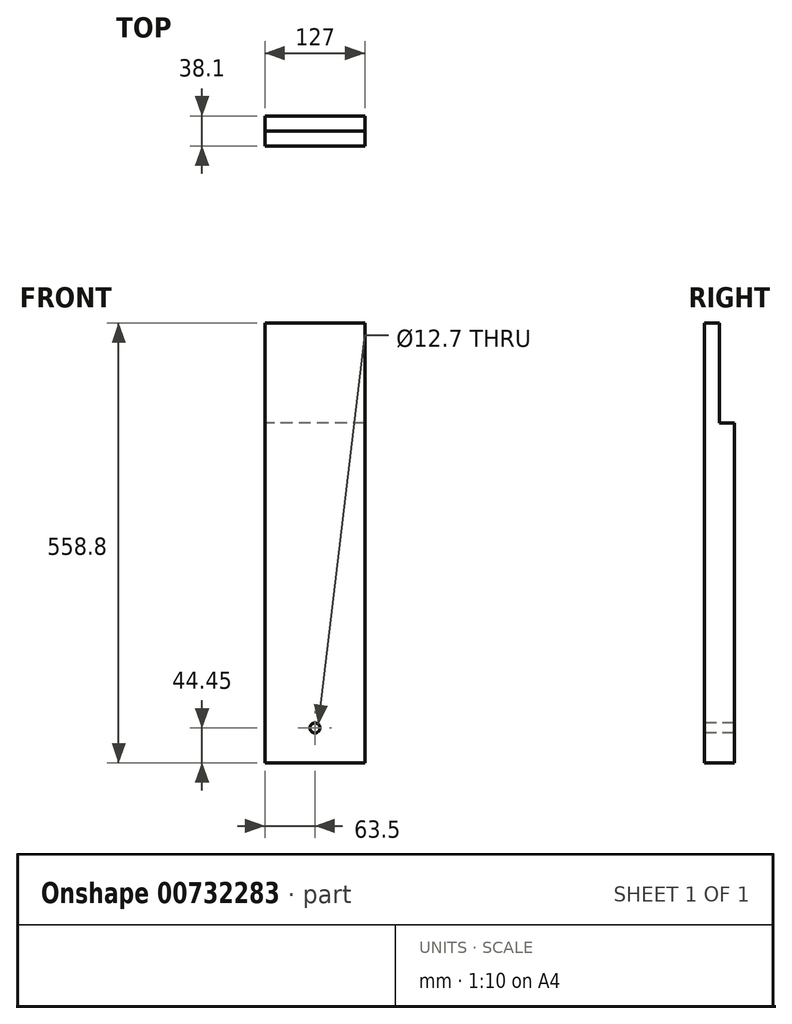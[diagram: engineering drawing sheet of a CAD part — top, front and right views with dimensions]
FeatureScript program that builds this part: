
annotation { "Feature Type Name" : "Feature", "Feature Type Description" : "" }
export const myFeature = defineFeature(function(context is Context, id is Id, definition is map)
    precondition{}
    {
        {
            var Q0;
            Q0=qCreatedBy(makeId("Front.planeOp"),FACE);
            var sketch = newSketch(context, id + "F0", { "sketchPlane" : qUnion([Q0])});
            skLineSegment(sketch, "E0.bottom", {"start": v(63.5, 279.4) * mm, "end": v(-63.5, 279.4) * mm});
            skLineSegment(sketch, "E0.top", {"start": v(63.5, -279.4) * mm, "end": v(-63.5, -279.4) * mm});
            skLineSegment(sketch, "E0.left", {"start": v(63.5, 279.4) * mm, "end": v(63.5, -279.4) * mm});
            skLineSegment(sketch, "E0.right", {"start": v(-63.5, 279.4) * mm, "end": v(-63.5, -279.4) * mm});
            skPoint(sketch, "E0.middle", {"position": v(0, 0) * mm});
            skSolve(sketch);
        }
        {
            var Q0;
            Q0 = qSketchRegion(id + "F0", true);
            extrude(context, id + "F1", {"entities" : qUnion([Q0]), "depth" : 38.1 * mm, "offsetDistance" : 25.4 * mm});
        }
        {
            var Q0;
            Q0=makeQuery(id+"F1.opExtrude","SWEPT_FACE",FACE,{"disambiguationData":[OSD([sQuery(id+"F0.wireOp",EDGE,"E0.right")])]});
            var sketch = newSketch(context, id + "F2", { "sketchPlane" : qUnion([Q0])});
            skLineSegment(sketch, "E1.bottom", {"start": v(19.05, 279.4) * mm, "end": v(0, 279.4) * mm});
            skLineSegment(sketch, "E1.top", {"start": v(19.05, 152.4) * mm, "end": v(0, 152.4) * mm});
            skLineSegment(sketch, "E1.left", {"start": v(19.05, 279.4) * mm, "end": v(19.05, 152.4) * mm});
            skLineSegment(sketch, "E1.right", {"start": v(0, 279.4) * mm, "end": v(0, 152.4) * mm});
            skSolve(sketch);
        }
        {
            var Q0;
            Q0 = qSketchRegion(id + "F2", true);
            extrude(context, id + "F3", {"entities" : qUnion([Q0]), "operationType" : NewBodyOperationType.REMOVE, "oppositeDirection" : true, "depth" : 152.4 * mm, "offsetDistance" : 25.4 * mm});
        }
        {
            var Q0;
            Q0=makeQuery(id+"F1.opExtrude","CAP_FACE",FACE,{"disambiguationData":[OSD([sQuery(id+"F0.wireOp",EDGE,"E0.bottom"),sQuery(id+"F0.wireOp",EDGE,"E0.top"),sQuery(id+"F0.wireOp",EDGE,"E0.left"),sQuery(id+"F0.wireOp",EDGE,"E0.right")])],"isStart":false});
            var sketch = newSketch(context, id + "F4", { "sketchPlane" : qUnion([Q0])});
            skLineSegment(sketch, "E2", {"start": v(0, 279.4) * mm, "end": v(0, -279.4) * mm, "construction": true});
            skLineSegment(sketch, "E3", {"start": v(-63.5, -234.95) * mm, "end": v(63.5, -234.95) * mm, "construction": true});
            skCircle(sketch, "E4", {"center": v(0, -234.95) * mm, "radius": 6.35 * mm});
            skSolve(sketch);
        }
        {
            var Q0;
            Q0=makeQuery(id+"F4.imprint","IMPRINT",FACE,{"disambiguationData":[TD([[makeQuery(id+"F4.imprint","IMPRINT",EDGE,{"derivedFrom":sQuery(id+"F4.wireOp",EDGE,"E4")}),1.0]])]});
            extrude(context, id + "F5", {"entities" : qUnion([Q0]), "operationType" : NewBodyOperationType.REMOVE, "endBound" : BoundingType.THROUGH_ALL, "oppositeDirection" : true, "depth" : 25.4 * mm, "offsetDistance" : 25.4 * mm});
        }
    });
